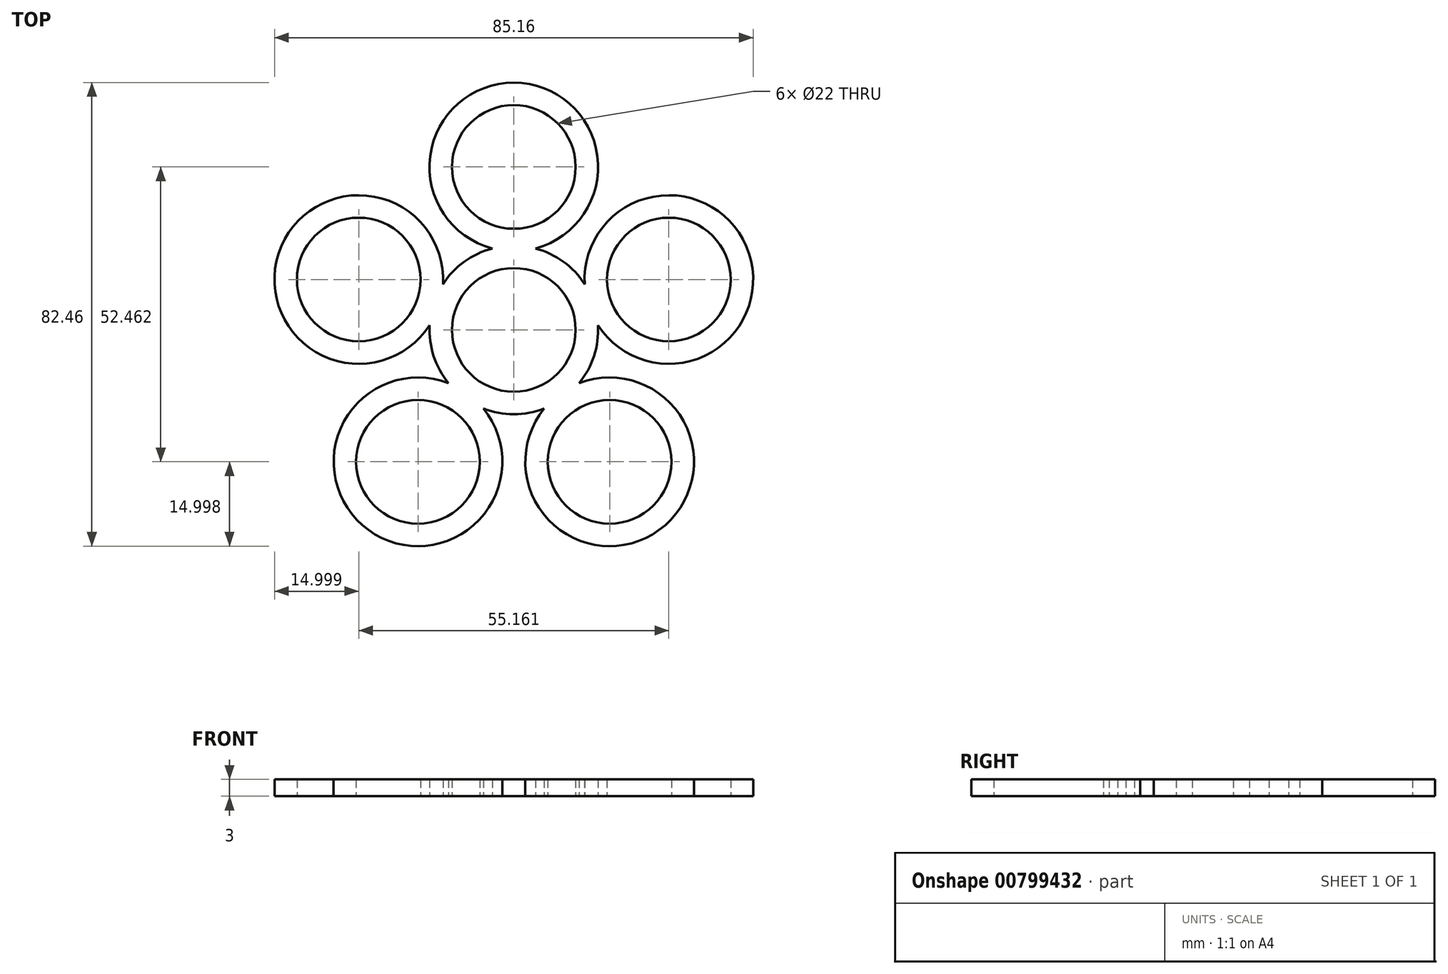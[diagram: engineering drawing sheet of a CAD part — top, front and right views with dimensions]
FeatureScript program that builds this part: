
annotation { "Feature Type Name" : "Feature", "Feature Type Description" : "" }
export const myFeature = defineFeature(function(context is Context, id is Id, definition is map)
    precondition{}
    {
        {
            var Q0;
            Q0=qCreatedBy(makeId("Top.planeOp"),FACE);
            var sketch = newSketch(context, id + "F0", { "sketchPlane" : qUnion([Q0])});
            skCircle(sketch, "E0", {"center": v(0, 0) * mm, "radius": 11 * mm});
            skLineSegment(sketch, "E1", {"start": v(0, 0) * mm, "end": v(0, 29) * mm});
            skCircle(sketch, "E2", {"center": v(0, 29) * mm, "radius": 11 * mm});
            skArc(sketch, "E3", {"start": v(-14.98, 0.83) * mm, "mid": v(-14.27, -4.64) * mm, "end": v(-11.63, -9.47) * mm});
            skArc(sketch, "E4", {"start": v(3.84, 14.5) * mm, "mid": v(0, 44) * mm, "end": v(-3.84, 14.5) * mm});
            skArc(sketch, "E5.1.0", {"start": v(-12.6, 8.13) * mm, "mid": v(-41.85, 13.6) * mm, "end": v(-14.98, 0.83) * mm});
            skCircle(sketch, "E5.1.1", {"center": v(-27.58, 8.96) * mm, "radius": 11 * mm});
            skArc(sketch, "E5.2.0", {"start": v(-11.63, -9.47) * mm, "mid": v(-25.86, -35.6) * mm, "end": v(-5.42, -13.99) * mm});
            skCircle(sketch, "E5.2.1", {"center": v(-17.05, -23.46) * mm, "radius": 11 * mm});
            skArc(sketch, "E5.3.0", {"start": v(5.42, -13.99) * mm, "mid": v(25.86, -35.6) * mm, "end": v(11.63, -9.47) * mm});
            skCircle(sketch, "E5.3.1", {"center": v(17.05, -23.46) * mm, "radius": 11 * mm});
            skArc(sketch, "E5.4.0", {"start": v(14.98, 0.83) * mm, "mid": v(41.85, 13.6) * mm, "end": v(12.6, 8.13) * mm});
            skCircle(sketch, "E5.4.1", {"center": v(27.58, 8.96) * mm, "radius": 11 * mm});
            skArc(sketch, "E6.trimOffspring", {"start": v(-3.84, 14.5) * mm, "mid": v(-8.82, 12.14) * mm, "end": v(-12.6, 8.13) * mm});
            skArc(sketch, "E7.trimOffspring", {"start": v(-5.42, -13.99) * mm, "mid": v(0, -15) * mm, "end": v(5.42, -13.99) * mm});
            skArc(sketch, "E8.trimOffspring", {"start": v(11.63, -9.47) * mm, "mid": v(14.27, -4.64) * mm, "end": v(14.98, 0.83) * mm});
            skArc(sketch, "E9.trimOffspring", {"start": v(12.6, 8.13) * mm, "mid": v(8.82, 12.14) * mm, "end": v(3.84, 14.5) * mm});
            skSolve(sketch);
        }
        {
            var Q0;
            Q0=makeQuery(id+"F0.imprint","IMPRINT",FACE,{"disambiguationData":[TD([[makeQuery(id+"F0.imprint","IMPRINT",EDGE,{"derivedFrom":sQuery(id+"F0.wireOp",EDGE,"E0")}),-1.0]])]});
            extrude(context, id + "F1", {"entities" : qUnion([Q0]), "depth" : 3 * mm, "offsetDistance" : 25 * mm});
        }
    });
